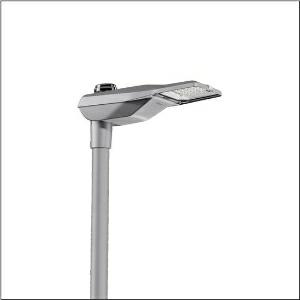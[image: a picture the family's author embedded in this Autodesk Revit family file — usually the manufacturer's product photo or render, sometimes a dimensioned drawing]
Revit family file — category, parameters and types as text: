
# Revit family: streetlight_sl_21_micro___st1_0a_5xe5d47n08cb_a602
name_source: partatom
category: Lighting Fixtures
units: mm (PartAtom-declared; Revit-internal decimal feet)

## family parameters
Cut with Voids When Loaded = No
Host = Face
Light Source = No
Part Type = Normal
Room Calculation Point = No
Round Connector Dimension = Use Diameter
Shared = No

## types (1)
- --- (1 x LED, 2380 lm, 15.8 W, 4000K)
    Apparent Load = 16 VA
    CIE Flux Codes = 37 72 97 100 100
    Color Rendering = 70
    Color Temperature = 4000K
    Default Elevation = 1800 mm
    Description = Streetlight SL 21 micro, mast luminaire, primary light control with lens, of PMMA, primary optical cover: cover, of toughened safety glass, transparent, light distribution: ST1.0a, light emission: direct distribution, primary light characteristic: asymmetric, installation type: post-top, LED, 3G 1.5mm², High Power LED, rated luminous flux: 2.380lm, luminous efficacy: 151lm/W, light colour: 740, colour temperature: 4000K, control gear: NEMA (7pin), control: overheat protection, pre-setting: linear dimming characteristic, constant luminous flux control, time-dependent luminous flux control, flexible luminous flux parameterisation, mains connection: 230..240V, AC, 50/60Hz, connection cable pre-assembled, cable length: 6,5m, wiring characteristics: H07RN-F, start of lifetime: 16W, end of service life: 16W, reduction: 8W, luminaire housing, of diecast aluminium (EN AC-44300), powder-coated, Siteco® metallic grey (DB 702S), corrosivity category C5 mid according to DIN EN ISO 12944, multi-level sealing system, sealing non-destructively replaceable, inclination adjustable: 0°, 5°, 10°, 15°, length: 528mm, width: 235mm, height: 110mm, spigot size: 76/60mm (post-top), mounting height: 4..8m, protection rating (complete): IP66, insulation class (complete): insulation class I (protective earthing), certification: CE, ENEC, ENEC+, VDE, impact resistance: IK10, permissible operating ambient temperature for outdoor applications: -40..+50°C, standard-compliant lighting for roads and squares, packaging unit: 1 piece

Light Distribution: ST1.0a
    Height = 110 mm
    Lamp = 1 x LED
    Lamp Light Flux = 2380 lm
    Lamp Power = 15.8 W
    Lamp count = 1
    Length = 528 mm
    Luminous efficacy = 151 lm/W
    Manufacturer = Siteco
    ModVariant = No
    Model = 5XE5D47N08CB
    Number of Poles = 1
    OnlyDefault = Yes
    Power Factor = 1
    Product Name = Streetlight SL 21 micro | ST1.0a
    Product group = mast luminaire | pylon top
    ProductGroupID = 6100
    Protection Class = Protection class I
    Protection Degree = IP 66
    RLX_Detail_Level = 1
    RLX_Emergency_Light_Flux = 0 lm
    RLX_Emergency_Type = 0
    RLX_Emergency_Type_DB = No
    RlxData = <blob elided: 98485 chars, md5=0f407590>
    Socket = socket
    Standby Power = 0 W
    System Light Flux = 2380 lm
    System Power = 16 W
    Type Comments = factory setting: luminous flux: 100 % | dim-lin: 254 | 300 mA
    Type Image = l_1294375.jpg
    URL = http://relux.com
    VarID = @adj_157993
    Voltage = 0 V
    Weight = 0.00 kg
    Width = 235 mm

## geometry (parser evidence)
native form markers: Blend x4, Sweep x11
no freeform markers — native parametric forms only
